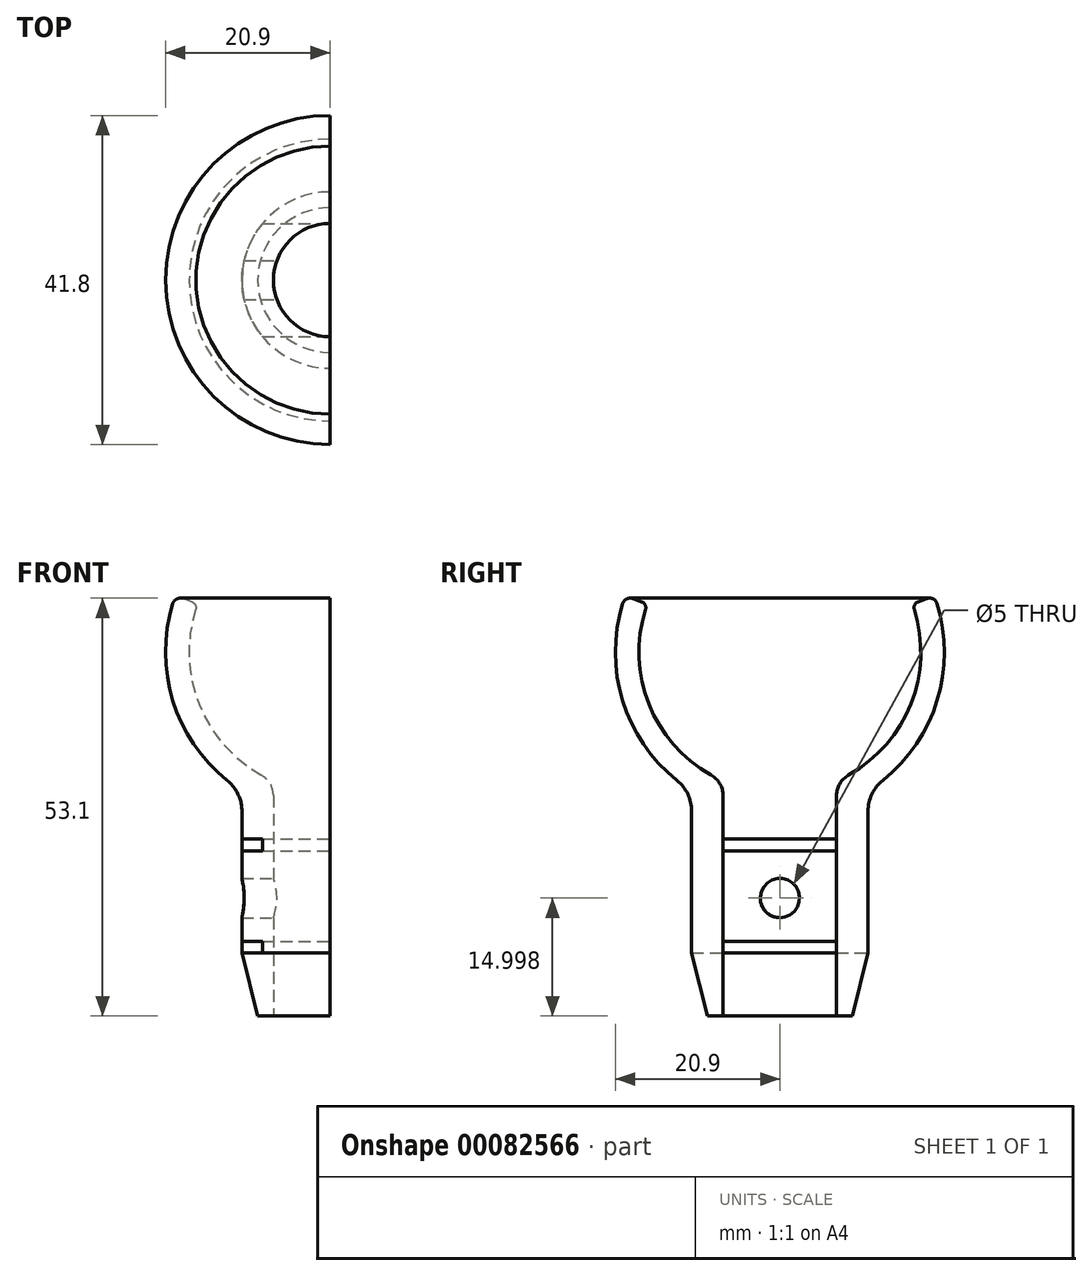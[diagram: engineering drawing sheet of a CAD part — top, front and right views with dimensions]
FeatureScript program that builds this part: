
annotation { "Feature Type Name" : "Feature", "Feature Type Description" : "" }
export const myFeature = defineFeature(function(context is Context, id is Id, definition is map)
    precondition{}
    {
        {
            var Q0;
            Q0=qCreatedBy(makeId("Front.planeOp"),FACE);
            var sketch = newSketch(context, id + "F0", { "sketchPlane" : qUnion([Q0])});
            skArc(sketch, "E0", {"start": v(-17.07, 5.4) * mm, "mid": v(-16.64, -6.6) * mm, "end": v(-8.74, -15.62) * mm});
            skLineSegment(sketch, "E1", {"start": v(0, 0) * mm, "end": v(-22.64, 8.24) * mm, "construction": true});
            skArc(sketch, "E2", {"start": v(-19.97, 6.15) * mm, "mid": v(-19.98, -6.14) * mm, "end": v(-13.07, -16.3) * mm});
            skLineSegment(sketch, "E3", {"start": v(0, 0) * mm, "end": v(0, 39.86) * mm, "construction": true});
            skLineSegment(sketch, "E4", {"start": v(-16.82, 6.12) * mm, "end": v(-16.82, 34.59) * mm, "construction": true});
            skLineSegment(sketch, "E5", {"start": v(0, 0) * mm, "end": v(0, -62.47) * mm, "construction": true});
            skLineSegment(sketch, "E6", {"start": v(-11.2, -20.2) * mm, "end": v(-11.2, -38.24) * mm});
            skLineSegment(sketch, "E7", {"start": v(-9.2, -46.24) * mm, "end": v(-7.2, -46.24) * mm});
            skLineSegment(sketch, "E8", {"start": v(-7.2, -46.24) * mm, "end": v(-7.2, -18.24) * mm});
            skPoint(sketch, "E9.visualSharp", {"position": v(-7.2, -16.39) * mm});
            skArc(sketch, "E9.filletArc", {"start": v(-7.2, -18.24) * mm, "mid": v(-7.61, -16.72) * mm, "end": v(-8.74, -15.62) * mm});
            skPoint(sketch, "E10.visualSharp", {"position": v(-11.2, -17.65) * mm});
            skArc(sketch, "E10.filletArc", {"start": v(-11.2, -20.2) * mm, "mid": v(-11.7, -18.04) * mm, "end": v(-13.07, -16.3) * mm});
            skLineSegment(sketch, "E11", {"start": v(-18.68, 6.8) * mm, "end": v(-17.56, 6.39) * mm});
            skPoint(sketch, "E12.visualSharp", {"position": v(-16.82, 6.12) * mm});
            skArc(sketch, "E12.filletArc", {"start": v(-17.07, 5.4) * mm, "mid": v(-17.11, 6) * mm, "end": v(-17.56, 6.39) * mm});
            skPoint(sketch, "E13.visualSharp", {"position": v(-19.64, 7.15) * mm});
            skArc(sketch, "E13.filletArc", {"start": v(-18.68, 6.8) * mm, "mid": v(-19.46, 6.75) * mm, "end": v(-19.97, 6.15) * mm});
            skLineSegment(sketch, "E14", {"start": v(-9.2, -46.24) * mm, "end": v(-11.2, -38.24) * mm});
            skPoint(sketch, "E15.orphan", {"position": v(-11.2, -46.24) * mm});
            skSolve(sketch);
        }
        {
            var Q0;
            Q0 = qSketchRegion(id + "F0", true);
            var Q1;
            Q1=sQuery(id+"F0.wireOp",EDGE,"E3");
            revolve(context, id + "F1", {"entities" : qUnion([Q0]), "axis" : qUnion([Q1]), "revolveType" : RevolveType.SYMMETRIC, "angle" : 180 * degree});
        }
        {
            var Q0;
            Q0=qCreatedBy(makeId("Right.planeOp"),FACE);
            var sketch = newSketch(context, id + "F2", { "sketchPlane" : qUnion([Q0])});
            skCircle(sketch, "E16", {"center": v(0, -31.24) * mm, "radius": 2.5 * mm});
            skSolve(sketch);
        }
        {
            var Q0;
            Q0 = qSketchRegion(id + "F2", true);
            extrude(context, id + "F3", {"entities" : qUnion([Q0]), "operationType" : NewBodyOperationType.REMOVE, "endBound" : BoundingType.THROUGH_ALL, "oppositeDirection" : true, "depth" : 25 * mm});
        }
        {
            var Q0;
            Q0=qCreatedBy(makeId("Right.planeOp"),FACE);
            var sketch = newSketch(context, id + "F4", { "sketchPlane" : qUnion([Q0])});
            skLineSegment(sketch, "E17.bottom", {"start": v(-7.2, -23.74) * mm, "end": v(7.2, -23.74) * mm});
            skLineSegment(sketch, "E17.top", {"start": v(-7.2, -25.24) * mm, "end": v(7.2, -25.24) * mm});
            skLineSegment(sketch, "E17.left", {"start": v(-7.2, -23.74) * mm, "end": v(-7.2, -25.24) * mm});
            skLineSegment(sketch, "E17.right", {"start": v(7.2, -23.74) * mm, "end": v(7.2, -25.24) * mm});
            skLineSegment(sketch, "E18.bottom", {"start": v(-7.2, -36.74) * mm, "end": v(7.2, -36.74) * mm});
            skLineSegment(sketch, "E18.top", {"start": v(-7.2, -38.24) * mm, "end": v(7.2, -38.24) * mm});
            skLineSegment(sketch, "E18.left", {"start": v(-7.2, -36.74) * mm, "end": v(-7.2, -38.24) * mm});
            skLineSegment(sketch, "E18.right", {"start": v(7.2, -36.74) * mm, "end": v(7.2, -38.24) * mm});
            skSolve(sketch);
        }
        {
            var Q0;
            Q0 = qSketchRegion(id + "F4", true);
            var Q1;
            Q1=makeQuery(id+"F1.opRevolve","SWEPT_FACE",FACE,{"disambiguationData":[OSD([sQuery(id+"F0.wireOp",EDGE,"E6")])]});
            extrude(context, id + "F5", {"entities" : qUnion([Q0]), "endBound" : BoundingType.UP_TO_SURFACE, "oppositeDirection" : true, "endBoundEntityFace" : qUnion([Q1]), "depth" : 25 * mm});
        }
    });
